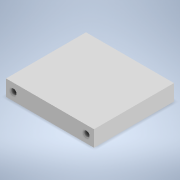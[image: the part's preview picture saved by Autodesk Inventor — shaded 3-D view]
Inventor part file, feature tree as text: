
AUTODESK INVENTOR PART (.ipt)
format: ipt  version: 2020 (Build 240168000, 168)  size: 108,032 bytes
history: native  units: in
note: dims shown in document units (in); Inventor stores cm internally (conversion verified against a paired STEP export)
features: other x3, reference x2, extrude x1, sketch x1
ambient origin geometry x8: Origin, YZ Plane, XZ Plane, XY Plane, X Axis, Y Axis, Z Axis, Center Point
bodies: Solid1 (feature_tree)
feature tree (7):
  extrude  "Extrusion1"  Depth=2.5in
  sketch  "Sketch1"  dims[d0=0.5in d3=0.25in d4=2.5in d5=0.0in]
  reference  "Reference1"
  reference  "Reference2"
  other  "<userpath>\Desktop\PnP Machine\PnP Machine.iam"
  other  "PnP Machine.iam"
  other  "YClamp:1"
